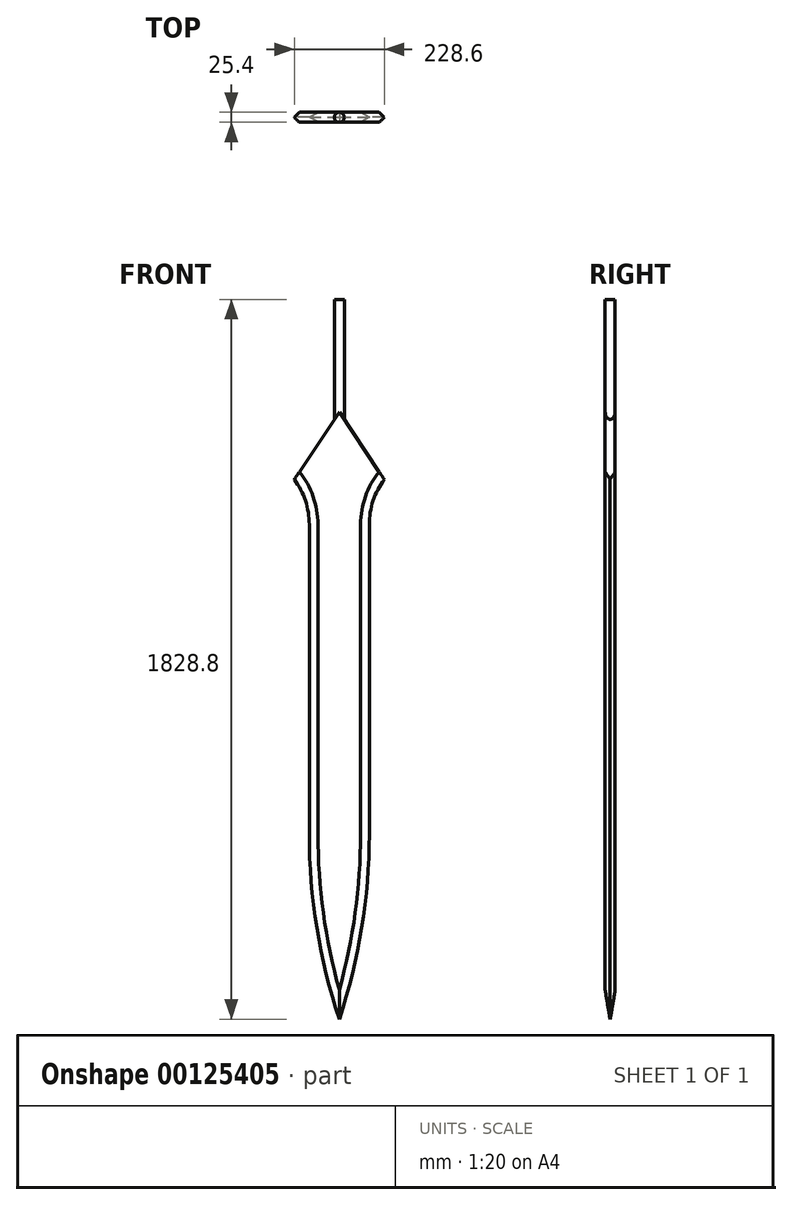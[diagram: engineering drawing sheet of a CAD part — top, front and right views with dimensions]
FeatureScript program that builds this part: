
annotation { "Feature Type Name" : "Feature", "Feature Type Description" : "" }
export const myFeature = defineFeature(function(context is Context, id is Id, definition is map)
    precondition{}
    {
        {
            var Q0;
            Q0=qCreatedBy(makeId("Front.planeOp"),FACE);
            var sketch = newSketch(context, id + "F0", { "sketchPlane" : qUnion([Q0])});
            skLineSegment(sketch, "E0", {"start": v(0, 0) * mm, "end": v(0, -914.4) * mm, "construction": true});
            skLineSegment(sketch, "E1", {"start": v(0, -914.4) * mm, "end": v(0, -914.4) * mm});
            skLineSegment(sketch, "E2", {"start": v(76.2, 406.4) * mm, "end": v(114.3, 457.2) * mm, "construction": true});
            skLineSegment(sketch, "E3", {"start": v(114.3, 457.2) * mm, "end": v(12.7, 609.6) * mm});
            skLineSegment(sketch, "E4", {"start": v(12.7, 609.6) * mm, "end": v(12.7, 914.4) * mm});
            skLineSegment(sketch, "E5", {"start": v(12.7, 914.4) * mm, "end": v(0, 914.4) * mm});
            skLineSegment(sketch, "E6", {"start": v(0, 914.4) * mm, "end": v(0, 0) * mm, "construction": true});
            skLineSegment(sketch, "E7.MirrorCS", {"start": v(-76.2, 406.4) * mm, "end": v(-114.3, 457.2) * mm, "construction": true});
            skLineSegment(sketch, "E8.MirrorCS", {"start": v(-114.3, 457.2) * mm, "end": v(-12.7, 609.6) * mm});
            skLineSegment(sketch, "E9.MirrorCS", {"start": v(-12.7, 609.6) * mm, "end": v(-12.7, 914.4) * mm});
            skLineSegment(sketch, "E10.MirrorCS", {"start": v(-12.7, 914.4) * mm, "end": v(0, 914.4) * mm});
            skLineSegment(sketch, "E11", {"start": v(-114.3, 457.2) * mm, "end": v(114.3, 457.2) * mm, "construction": true});
            skLineSegment(sketch, "E12", {"start": v(12.7, 609.6) * mm, "end": v(-12.7, 609.6) * mm, "construction": true});
            skLineSegment(sketch, "E13", {"start": v(-76.2, 406.4) * mm, "end": v(76.2, 406.4) * mm, "construction": true});
            skLineSegment(sketch, "E14", {"start": v(-76.2, 406.4) * mm, "end": v(-76.2, -685.8) * mm, "construction": true});
            skLineSegment(sketch, "E15", {"start": v(-76.2, -685.8) * mm, "end": v(0, -914.4) * mm, "construction": true});
            skLineSegment(sketch, "E16", {"start": v(0, -914.4) * mm, "end": v(76.2, -685.8) * mm, "construction": true});
            skLineSegment(sketch, "E17", {"start": v(76.2, -685.8) * mm, "end": v(76.2, 406.4) * mm, "construction": true});
            skLineSegment(sketch, "E18", {"start": v(-76.2, -685.8) * mm, "end": v(76.2, -685.8) * mm, "construction": true});
            skLineSegment(sketch, "E19", {"start": v(0, -914.4) * mm, "end": v(76.2, -914.4) * mm, "construction": true});
            skLineSegment(sketch, "E20", {"start": v(76.2, -914.4) * mm, "end": v(76.2, -685.8) * mm, "construction": true});
            skArc(sketch, "E21", {"start": v(0, -914.4) * mm, "mid": v(57.03, -682.69) * mm, "end": v(76.2, -444.83) * mm});
            skArc(sketch, "E22", {"start": v(-76.2, -444.83) * mm, "mid": v(-57.03, -682.69) * mm, "end": v(0, -914.4) * mm});
            skLineSegment(sketch, "E23", {"start": v(-76.2, -444.83) * mm, "end": v(76.2, -444.83) * mm, "construction": true});
            skLineSegment(sketch, "E24", {"start": v(-76.2, -444.83) * mm, "end": v(-76.2, 342.9) * mm});
            skLineSegment(sketch, "E25", {"start": v(76.2, -444.83) * mm, "end": v(76.2, 342.9) * mm});
            skArc(sketch, "E26", {"start": v(-76.2, 342.9) * mm, "mid": v(-85.98, 403.14) * mm, "end": v(-114.3, 457.2) * mm});
            skArc(sketch, "E27", {"start": v(114.3, 457.2) * mm, "mid": v(85.98, 403.14) * mm, "end": v(76.2, 342.9) * mm});
            skSolve(sketch);
        }
        {
            var Q0;
            Q0 = qSketchRegion(id + "F0", true);
            extrude(context, id + "F1", {"entities" : qUnion([Q0]), "depth" : 25.4 * mm});
        }
        {
            var Q0;
            Q0=makeQuery(id+"F1.opExtrude","CAP_EDGE",EDGE,{"disambiguationData":[OSD([sQuery(id+"F0.wireOp",EDGE,"E24")])],"isStart":false});
            var Q1;
            Q1=makeQuery(id+"F1.opExtrude","CAP_EDGE",EDGE,{"disambiguationData":[OSD([sQuery(id+"F0.wireOp",EDGE,"E25")])],"isStart":false});
            var Q2;
            Q2=makeQuery(id+"F1.opExtrude","CAP_EDGE",EDGE,{"disambiguationData":[OSD([sQuery(id+"F0.wireOp",EDGE,"E24")])],"isStart":true});
            var Q3;
            Q3=makeQuery(id+"F1.opExtrude","CAP_EDGE",EDGE,{"disambiguationData":[OSD([sQuery(id+"F0.wireOp",EDGE,"E25")])],"isStart":true});
            chamfer(context, id + "F2", {"entities" : qUnion([Q0, Q1, Q2, Q3]), "chamferType" : ChamferType.OFFSET_ANGLE, "width" : 12.7 * mm, "oppositeDirection" : false, "angle" : 60 * degree, "tangentPropagation" : true});
        }
        {
            var Q0;
            Q0=makeQuery(id+"F1.opExtrude","CAP_EDGE",EDGE,{"disambiguationData":[OSD([sQuery(id+"F0.wireOp",EDGE,"E9.MirrorCS")])],"isStart":false});
            var Q1;
            Q1=makeQuery(id+"F1.opExtrude","CAP_EDGE",EDGE,{"disambiguationData":[OSD([sQuery(id+"F0.wireOp",EDGE,"E4")])],"isStart":false});
            var Q2;
            Q2=makeQuery(id+"F1.opExtrude","CAP_EDGE",EDGE,{"disambiguationData":[OSD([sQuery(id+"F0.wireOp",EDGE,"E4")])],"isStart":true});
            var Q3;
            Q3=makeQuery(id+"F1.opExtrude","CAP_EDGE",EDGE,{"disambiguationData":[OSD([sQuery(id+"F0.wireOp",EDGE,"E9.MirrorCS")])],"isStart":true});
            fillet(context, id + "F3", {"entities" : qUnion([Q0, Q1, Q2, Q3]), "radius" : 12.7 * mm, "tangentPropagation" : true, "allowEdgeOverflow" : false});
        }
    });
